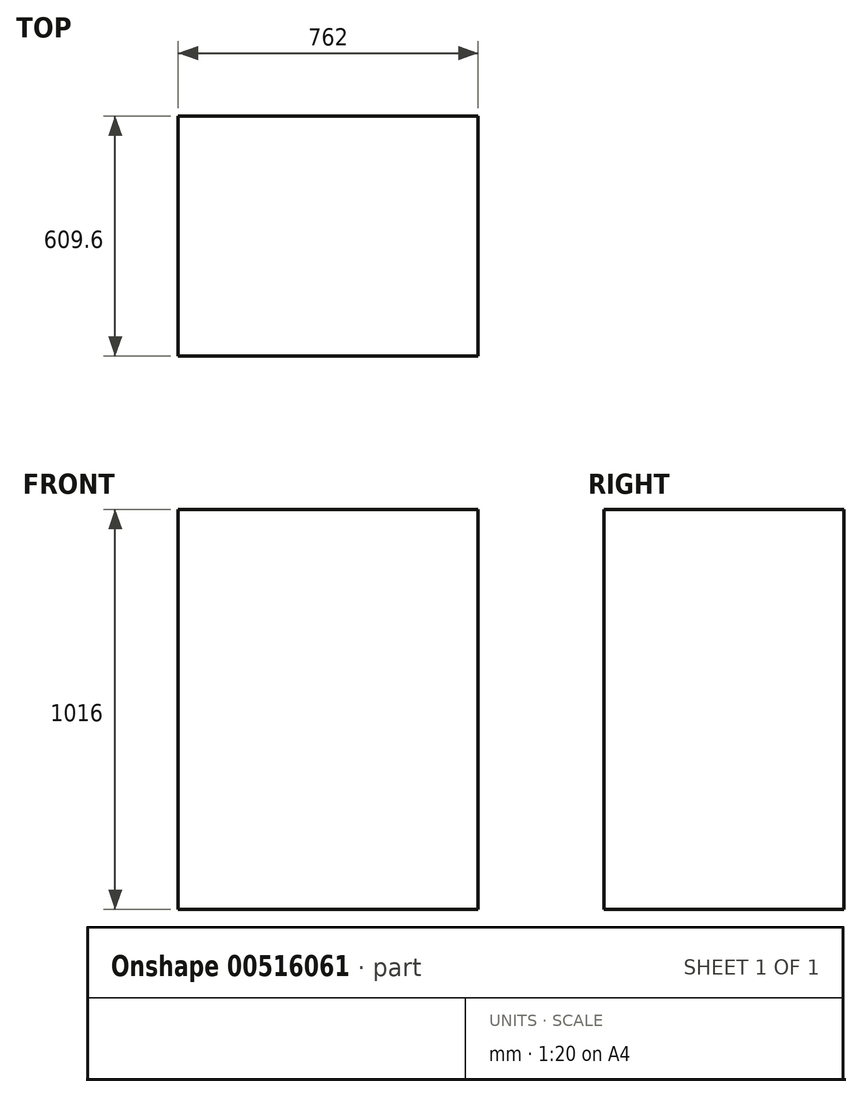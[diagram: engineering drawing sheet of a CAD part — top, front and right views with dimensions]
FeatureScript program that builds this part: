
annotation { "Feature Type Name" : "Feature", "Feature Type Description" : "" }
export const myFeature = defineFeature(function(context is Context, id is Id, definition is map)
    precondition{}
    {
        {
            var Q0;
            Q0=qCreatedBy(makeId("Front.planeOp"),FACE);
            var sketch = newSketch(context, id + "F0", { "sketchPlane" : qUnion([Q0])});
            skLineSegment(sketch, "E0.bottom", {"start": v(381, -508) * mm, "end": v(-381, -508) * mm});
            skLineSegment(sketch, "E0.top", {"start": v(381, 508) * mm, "end": v(-381, 508) * mm});
            skLineSegment(sketch, "E0.left", {"start": v(381, -508) * mm, "end": v(381, 508) * mm});
            skLineSegment(sketch, "E0.right", {"start": v(-381, -508) * mm, "end": v(-381, 508) * mm});
            skPoint(sketch, "E0.middle", {"position": v(0, 0) * mm});
            skSolve(sketch);
        }
        {
            var Q0;
            Q0=makeQuery(id+"F0.imprint","IMPRINT",FACE,{"disambiguationData":[TD([[makeQuery(id+"F0.imprint","IMPRINT",EDGE,{"derivedFrom":sQuery(id+"F0.wireOp",EDGE,"E0.bottom")}),-1.0]])]});
            extrude(context, id + "F1", {"entities" : qUnion([Q0]), "depth" : 609.6 * mm, "offsetDistance" : 25.4 * mm});
        }
    });
